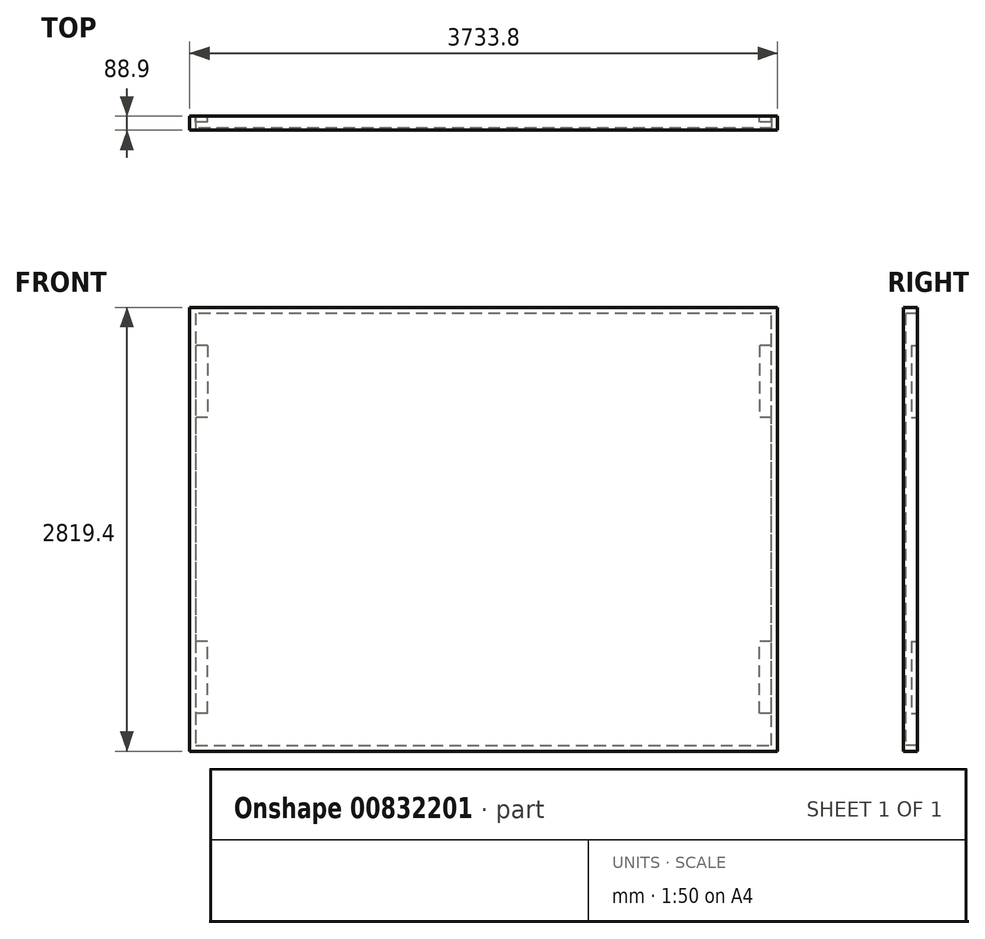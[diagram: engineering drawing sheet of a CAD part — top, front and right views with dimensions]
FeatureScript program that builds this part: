
annotation { "Feature Type Name" : "Feature", "Feature Type Description" : "" }
export const myFeature = defineFeature(function(context is Context, id is Id, definition is map)
    precondition{}
    {
        {
            var Q0;
            Q0=qCreatedBy(makeId("Front.planeOp"),FACE);
            var sketch = newSketch(context, id + "F0", { "sketchPlane" : qUnion([Q0])});
            skLineSegment(sketch, "E0.bottom", {"start": v(1866.9, 1409.7) * mm, "end": v(-1866.9, 1409.7) * mm});
            skLineSegment(sketch, "E0.left", {"start": v(1866.9, 1409.7) * mm, "end": v(1866.9, -1409.7) * mm});
            skLineSegment(sketch, "E0.right", {"start": v(-1866.9, 1409.7) * mm, "end": v(-1866.9, -1409.7) * mm});
            skPoint(sketch, "E0.middle", {"position": v(0, 0) * mm});
            skLineSegment(sketch, "E1.trimOffspring", {"start": v(1866.9, -1409.7) * mm, "end": v(-1866.9, -1409.7) * mm});
            skSolve(sketch);
        }
        {
            var Q0;
            Q0=qSketchRegion(id+"F0",true);
            extrude(context, id + "F1", {"entities" : qUnion([Q0]), "depth" : 12.7 * mm, "offsetDistance" : 25.4 * mm});
        }
        {
            var Q0;
            Q0=makeQuery(id+"F1.opExtrude","CAP_FACE",FACE,{"disambiguationData":[OSD([sQuery(id+"F0.wireOp",EDGE,"E0.bottom"),sQuery(id+"F0.wireOp",EDGE,"E0.left"),sQuery(id+"F0.wireOp",EDGE,"E0.right"),sQuery(id+"F0.wireOp",EDGE,"E1.trimOffspring")])],"isStart":true});
            var sketch = newSketch(context, id + "F2", { "sketchPlane" : qUnion([Q0])});
            skLineSegment(sketch, "E2.bottom", {"start": v(-1866.9, 1409.7) * mm, "end": v(1866.9, 1409.7) * mm});
            skLineSegment(sketch, "E2.top", {"start": v(-1866.9, 1371.6) * mm, "end": v(1866.9, 1371.6) * mm});
            skLineSegment(sketch, "E2.left", {"start": v(-1866.9, 1409.7) * mm, "end": v(-1866.9, 1371.6) * mm});
            skLineSegment(sketch, "E2.right", {"start": v(1866.9, 1409.7) * mm, "end": v(1866.9, 1371.6) * mm});
            skLineSegment(sketch, "E3.bottom", {"start": v(1866.9, 1371.6) * mm, "end": v(1828.8, 1371.6) * mm});
            skLineSegment(sketch, "E3.top", {"start": v(1866.9, -1371.6) * mm, "end": v(1828.8, -1371.6) * mm});
            skLineSegment(sketch, "E3.left", {"start": v(1866.9, 1371.6) * mm, "end": v(1866.9, -1371.6) * mm});
            skLineSegment(sketch, "E3.right", {"start": v(1828.8, 1371.6) * mm, "end": v(1828.8, -1371.6) * mm});
            skLineSegment(sketch, "E4.bottom", {"start": v(1866.9, -1371.6) * mm, "end": v(-1866.9, -1371.6) * mm});
            skLineSegment(sketch, "E4.top", {"start": v(1866.9, -1409.7) * mm, "end": v(-1866.9, -1409.7) * mm});
            skLineSegment(sketch, "E4.left", {"start": v(1866.9, -1371.6) * mm, "end": v(1866.9, -1409.7) * mm});
            skLineSegment(sketch, "E4.right", {"start": v(-1866.9, -1371.6) * mm, "end": v(-1866.9, -1409.7) * mm});
            skLineSegment(sketch, "E5.bottom", {"start": v(-1866.9, -1371.6) * mm, "end": v(-1828.8, -1371.6) * mm});
            skLineSegment(sketch, "E5.top", {"start": v(-1866.9, 1371.6) * mm, "end": v(-1828.8, 1371.6) * mm});
            skLineSegment(sketch, "E5.left", {"start": v(-1866.9, -1371.6) * mm, "end": v(-1866.9, 1371.6) * mm});
            skLineSegment(sketch, "E5.right", {"start": v(-1828.8, -1371.6) * mm, "end": v(-1828.8, 1371.6) * mm});
            skLineSegment(sketch, "E6.bottom", {"start": v(-1752.6, 1371.6) * mm, "end": v(-1714.5, 1371.6) * mm});
            skLineSegment(sketch, "E6.top", {"start": v(-1752.6, -1371.6) * mm, "end": v(-1714.5, -1371.6) * mm});
            skLineSegment(sketch, "E6.left", {"start": v(-1752.6, 1371.6) * mm, "end": v(-1752.6, -1371.6) * mm});
            skLineSegment(sketch, "E6.right", {"start": v(-1714.5, 1371.6) * mm, "end": v(-1714.5, -1371.6) * mm});
            skLineSegment(sketch, "E7.bottom", {"start": v(1752.6, 1371.6) * mm, "end": v(1714.5, 1371.6) * mm});
            skLineSegment(sketch, "E7.top", {"start": v(1752.6, -1371.6) * mm, "end": v(1714.5, -1371.6) * mm});
            skLineSegment(sketch, "E7.left", {"start": v(1752.6, 1371.6) * mm, "end": v(1752.6, -1371.6) * mm});
            skLineSegment(sketch, "E7.right", {"start": v(1714.5, 1371.6) * mm, "end": v(1714.5, -1371.6) * mm});
            skLineSegment(sketch, "E8.bottom", {"start": v(1181.1, -1371.6) * mm, "end": v(1143, -1371.6) * mm});
            skLineSegment(sketch, "E8.top", {"start": v(1181.1, 1371.6) * mm, "end": v(1143, 1371.6) * mm});
            skLineSegment(sketch, "E8.left", {"start": v(1181.1, -1371.6) * mm, "end": v(1181.1, 1371.6) * mm});
            skLineSegment(sketch, "E8.right", {"start": v(1143, -1371.6) * mm, "end": v(1143, 1371.6) * mm});
            skLineSegment(sketch, "E9.bottom", {"start": v(609.6, 1371.6) * mm, "end": v(571.5, 1371.6) * mm});
            skLineSegment(sketch, "E9.top", {"start": v(609.6, -1371.6) * mm, "end": v(571.5, -1371.6) * mm});
            skLineSegment(sketch, "E9.left", {"start": v(609.6, 1371.6) * mm, "end": v(609.6, -1371.6) * mm});
            skLineSegment(sketch, "E9.right", {"start": v(571.5, 1371.6) * mm, "end": v(571.5, -1371.6) * mm});
            skLineSegment(sketch, "E10.bottom", {"start": v(69.85, -1371.6) * mm, "end": v(31.75, -1371.6) * mm});
            skLineSegment(sketch, "E10.top", {"start": v(69.85, 1371.6) * mm, "end": v(31.75, 1371.6) * mm});
            skLineSegment(sketch, "E10.left", {"start": v(69.85, -1371.6) * mm, "end": v(69.85, 1371.6) * mm});
            skLineSegment(sketch, "E10.right", {"start": v(31.75, -1371.6) * mm, "end": v(31.75, 1371.6) * mm});
            skLineSegment(sketch, "E11.bottom", {"start": v(-571.5, 1371.6) * mm, "end": v(-609.6, 1371.6) * mm});
            skLineSegment(sketch, "E11.top", {"start": v(-571.5, -1371.6) * mm, "end": v(-609.6, -1371.6) * mm});
            skLineSegment(sketch, "E11.left", {"start": v(-571.5, 1371.6) * mm, "end": v(-571.5, -1371.6) * mm});
            skLineSegment(sketch, "E11.right", {"start": v(-609.6, 1371.6) * mm, "end": v(-609.6, -1371.6) * mm});
            skLineSegment(sketch, "E12.bottom", {"start": v(-1143, -1371.6) * mm, "end": v(-1181.1, -1371.6) * mm});
            skLineSegment(sketch, "E12.top", {"start": v(-1143, 1371.6) * mm, "end": v(-1181.1, 1371.6) * mm});
            skLineSegment(sketch, "E12.left", {"start": v(-1143, -1371.6) * mm, "end": v(-1143, 1371.6) * mm});
            skLineSegment(sketch, "E12.right", {"start": v(-1181.1, -1371.6) * mm, "end": v(-1181.1, 1371.6) * mm});
            skSolve(sketch);
        }
        {
            var Q0;
            Q0=qSketchRegion(id+"F2",true);
            var Q1;
            Q1=makeQuery(id+"F2.imprint","IMPRINT",FACE,{"disambiguationData":[TD([[makeQuery(id+"F2.imprint","IMPRINT",EDGE,{"derivedFrom":sQuery(id+"F2.wireOp",EDGE,"E6.bottom")}),-1.0]])]});
            var Q2;
            Q2=makeQuery(id+"F2.imprint","IMPRINT",FACE,{"disambiguationData":[TD([[makeQuery(id+"F2.imprint","IMPRINT",EDGE,{"derivedFrom":sQuery(id+"F2.wireOp",EDGE,"E12.bottom")}),-1.0]])]});
            var Q3;
            Q3=makeQuery(id+"F2.imprint","IMPRINT",FACE,{"disambiguationData":[TD([[makeQuery(id+"F2.imprint","IMPRINT",EDGE,{"derivedFrom":sQuery(id+"F2.wireOp",EDGE,"E11.bottom")}),1.0]])]});
            var Q4;
            Q4=makeQuery(id+"F2.imprint","IMPRINT",FACE,{"disambiguationData":[TD([[makeQuery(id+"F2.imprint","IMPRINT",EDGE,{"derivedFrom":sQuery(id+"F2.wireOp",EDGE,"E10.bottom")}),-1.0]])]});
            var Q5;
            Q5=makeQuery(id+"F2.imprint","IMPRINT",FACE,{"disambiguationData":[TD([[makeQuery(id+"F2.imprint","IMPRINT",EDGE,{"derivedFrom":sQuery(id+"F2.wireOp",EDGE,"E9.bottom")}),1.0]])]});
            var Q6;
            Q6=makeQuery(id+"F2.imprint","IMPRINT",FACE,{"disambiguationData":[TD([[makeQuery(id+"F2.imprint","IMPRINT",EDGE,{"derivedFrom":sQuery(id+"F2.wireOp",EDGE,"E8.bottom")}),-1.0]])]});
            var Q7;
            Q7=makeQuery(id+"F2.imprint","IMPRINT",FACE,{"disambiguationData":[TD([[makeQuery(id+"F2.imprint","IMPRINT",EDGE,{"derivedFrom":sQuery(id+"F2.wireOp",EDGE,"E7.bottom")}),1.0]])]});
            extrude(context, id + "F3", {"entities" : qUnion([Q0, Q1, Q2, Q3, Q4, Q5, Q6, Q7]), "operationType" : NewBodyOperationType.ADD, "depth" : 76.2 * mm, "offsetDistance" : 25.4 * mm});
        }
        {
            var Q0;
            Q0=makeQuery(id+"F3.opExtrude","CAP_FACE",FACE,{"disambiguationData":[OSD([sQuery(id+"F2.wireOp",EDGE,"E2.bottom"),sQuery(id+"F2.wireOp",EDGE,"E2.top"),sQuery(id+"F2.wireOp",EDGE,"E2.left"),sQuery(id+"F2.wireOp",EDGE,"E2.right"),sQuery(id+"F2.wireOp",EDGE,"E3.left"),sQuery(id+"F2.wireOp",EDGE,"E3.right"),sQuery(id+"F2.wireOp",EDGE,"E4.bottom"),sQuery(id+"F2.wireOp",EDGE,"E4.top"),sQuery(id+"F2.wireOp",EDGE,"E4.left"),sQuery(id+"F2.wireOp",EDGE,"E4.right"),sQuery(id+"F2.wireOp",EDGE,"E5.left"),sQuery(id+"F2.wireOp",EDGE,"E5.right"),sQuery(id+"F2.wireOp",EDGE,"E6.left"),sQuery(id+"F2.wireOp",EDGE,"E6.right"),sQuery(id+"F2.wireOp",EDGE,"E7.left"),sQuery(id+"F2.wireOp",EDGE,"E7.right"),sQuery(id+"F2.wireOp",EDGE,"E8.left"),sQuery(id+"F2.wireOp",EDGE,"E8.right"),sQuery(id+"F2.wireOp",EDGE,"E9.left"),sQuery(id+"F2.wireOp",EDGE,"E9.right"),sQuery(id+"F2.wireOp",EDGE,"E10.left"),sQuery(id+"F2.wireOp",EDGE,"E10.right"),sQuery(id+"F2.wireOp",EDGE,"E11.left"),sQuery(id+"F2.wireOp",EDGE,"E11.right"),sQuery(id+"F2.wireOp",EDGE,"E12.left"),sQuery(id+"F2.wireOp",EDGE,"E12.right")])],"isStart":false});
            var sketch = newSketch(context, id + "F4", { "sketchPlane" : qUnion([Q0])});
            skLineSegment(sketch, "E13.bottom", {"start": v(-1828.8, 1168.4) * mm, "end": v(-1752.6, 1168.4) * mm});
            skLineSegment(sketch, "E13.top", {"start": v(-1828.8, 711.2) * mm, "end": v(-1752.6, 711.2) * mm});
            skLineSegment(sketch, "E13.left", {"start": v(-1828.8, 1168.4) * mm, "end": v(-1828.8, 711.2) * mm});
            skLineSegment(sketch, "E13.right", {"start": v(-1752.6, 1168.4) * mm, "end": v(-1752.6, 711.2) * mm});
            skLineSegment(sketch, "E14.bottom", {"start": v(-1828.8, -1168.4) * mm, "end": v(-1752.6, -1168.4) * mm});
            skLineSegment(sketch, "E14.top", {"start": v(-1828.8, -711.2) * mm, "end": v(-1752.6, -711.2) * mm});
            skLineSegment(sketch, "E14.left", {"start": v(-1828.8, -1168.4) * mm, "end": v(-1828.8, -711.2) * mm});
            skLineSegment(sketch, "E14.right", {"start": v(-1752.6, -1168.4) * mm, "end": v(-1752.6, -711.2) * mm});
            skLineSegment(sketch, "E15.bottom", {"start": v(1752.6, 1168.4) * mm, "end": v(1828.8, 1168.4) * mm});
            skLineSegment(sketch, "E15.top", {"start": v(1752.6, 711.2) * mm, "end": v(1828.8, 711.2) * mm});
            skLineSegment(sketch, "E15.left", {"start": v(1752.6, 1168.4) * mm, "end": v(1752.6, 711.2) * mm});
            skLineSegment(sketch, "E15.right", {"start": v(1828.8, 1168.4) * mm, "end": v(1828.8, 711.2) * mm});
            skLineSegment(sketch, "E16.bottom", {"start": v(1752.6, -1168.4) * mm, "end": v(1828.8, -1168.4) * mm});
            skLineSegment(sketch, "E16.top", {"start": v(1752.6, -711.2) * mm, "end": v(1828.8, -711.2) * mm});
            skLineSegment(sketch, "E16.left", {"start": v(1752.6, -1168.4) * mm, "end": v(1752.6, -711.2) * mm});
            skLineSegment(sketch, "E16.right", {"start": v(1828.8, -1168.4) * mm, "end": v(1828.8, -711.2) * mm});
            skSolve(sketch);
        }
        {
            var Q0;
            Q0=qSketchRegion(id+"F4",true);
            extrude(context, id + "F5", {"entities" : qUnion([Q0]), "operationType" : NewBodyOperationType.ADD, "oppositeDirection" : true, "depth" : 38.1 * mm, "offsetDistance" : 25.4 * mm});
        }
    });
